# Revit family: Hager-Orion_Inox-IP66-D250-Cl.I-Inox_encl-630A-600mm-NoHosted-CH-fr
name_source: partatom
category: Equipement électrique
units: mm (PartAtom-declared; Revit-internal decimal feet)

## family parameters
Basée sur le plan de construction = Oui
Configuration du panneau = Deux colonnes, circuits au sein
Cote de connecteur circulaire = Utiliser le diamètre
Couper avec des vides une fois chargée = Non
Partagée = Non
Point de calcul de pièce = Non
Toujours verticalement = Oui
Type d'élément = Tableau de raccordement

## types (4) — shared parameters
Commentaires du type = Orion Inox
EF000003 - mode de pose = EV000384 - saillie
EF000007 - couleur = EV000154 - autre
EF000040 - hauteur = 600 mm
EF000049 - profondeur = 250 mm  [stored 0.82021 ft]
EF000118 - avec cadre/support de montage = Non
EF000339 - type de capot = EV004216 - porte
EF001088 - possibilité de montage en saillie = Oui
EF001131 - profondeur intérieure = 216 mm  [stored 0.708661 ft]
EF001596 - matériau du boîtier/corps = EV000166 - acier inoxydable
EF003532 - convient pour utilisation à l’extérieur = Oui
EF004464 - type de porte = EV002646 - unique
EF005474 - indice de protection (IP) = EV006422 - IP66
EF007800 - adapté à un parafoudre = Non
EF008873 - courant nominal (In) = 630 A
EF009170 - épaisseur de matériau du boîtier = 2 mm  [stored 0.00656168 ft]
EF009171 - épaisseur de matériau de la porte/du couvercle = 2 mm  [stored 0.00656168 ft]
EF015940 - couvercle avec décharge de pression = Non
Elévation par défaut = 1219 mm
Fabricant = Hager
HG000002 - avec porte = Oui
HG000003 - Gamme = Orion Inox
HG000006 - Encastré = Non
HG000009 - Porte à double battant = Non
HG000010 - Portes asymétriques = Non
HG000023 - Armoire double section = Non
HG000024 - Hauteur de la section basse = 600 mm
HG000026 - Installation au sol = Non
zero-valued in all types: EF000218 - profondeur d'encastrement, EF000266 - nombre de rangées, EF000437 - nombre d'entrées de conduit, EF002950 - largeur en nombre de modules, EF004427 - nombre de modules, EF009554 - nombre d'ouvertures pour plaques à bride, HG000027 - Hauteur du socle

## per-type parameters (varying)
| type | EF000008 - largeur | EF001613 - maintien de fonction | EF004293 - indice de protection contre les chocs (IK) | EF006244 - couvercle/porte transparent(e) | EF006306 - avec serrure | EF009212 - finition du couvercle | HG000004 - Référence fabricant |
| saillie IP66 L400 H600 P250  - FL029BW | 400 mm  [stored 1.31234 ft] |  | EV008784 - IK10 | Non | Non | EV009916 - avec échancrure | FL029BW |
| saillie IP66 L600 H600 P250  - FL029BWL | 600 mm |  | EV008784 - IK10 | Non | Non | EV009916 - avec échancrure | FL029BWL |
| saillie IP66 L600 H600 P250  - FL029TW | 600 mm | EV000494 - sans | EV006814 - IK08 | Oui | Oui | EV000116 - fermé | FL029TW |
| saillie IP66 L600 H600 P250  - FL029TWL | 600 mm | EV000494 - sans | EV006814 - IK08 | Oui | Oui | EV000116 - fermé | FL029TWL |

note: [stored X ft] marks values corroborated as IEEE doubles in the binary element streams (Revit-internal decimal feet)

## geometry (parser evidence)
native form markers: Blend x4, Sweep x8
no freeform markers — native parametric forms only
